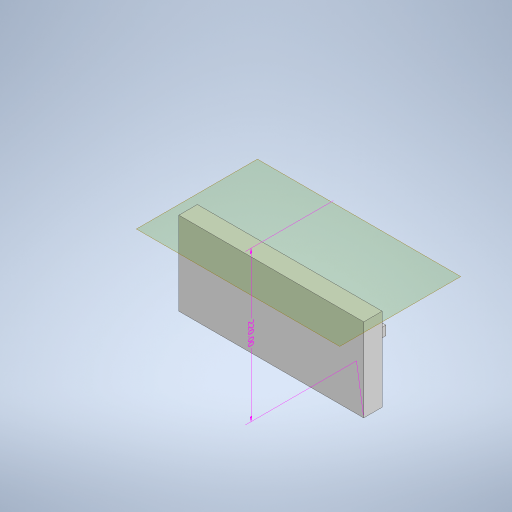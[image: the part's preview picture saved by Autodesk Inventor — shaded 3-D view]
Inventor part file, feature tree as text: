
AUTODESK INVENTOR PART (.ipt)
format: ipt  version: 2023 (Build 270158000, 158)  size: 312,832 bytes
history: native  units: mm
features: extrude x6, sketch x6, other x4, plane x3, split x1
ambient origin geometry x8: Origin, YZ Plane, XZ Plane, XY Plane, X Axis, Y Axis, Z Axis, Center Point
bodies: Body1 (feature_tree), Body2 (feature_tree)
feature tree (20):
  other  "Sólido1"
  other  "Anotaciones"
  extrude  "Extrusión1"  Depth=80.0mm
  extrude  "Extrusión2"  Depth=180.0mm
  extrude  "Extrusión3"  Depth=20.0mm
  extrude  "Extrusión4"  Depth=21.0mm
  plane  "Plano de trabajo1"
  extrude  "Extrusión6"  Depth=20.0mm
  plane  "Plano de trabajo3"
  extrude  "Extrusión7"  [1 undecoded]
  plane  "Plano de trabajo4"
  split  "Dividir1"
  sketch  "Boceto1"  dims[d0=200.0mm d1=80.0mm]
  sketch  "Boceto2"  dims[d2=130.0mm d3=0.0mm d4=180.0mm]
  sketch  "Boceto3"  dims[d5=60.0mm d6=20.0mm]
  sketch  "Boceto4"  dims[d7=60.0mm d8=0.0mm d9=21.0mm d10=43.0mm]
  sketch  "Boceto7"  dims[d11=43.0mm d12=0.0mm d13=20.0mm]
  other  "Sólido3"
  sketch  "Boceto10"  dims[d14=90.0mm d15=0.0mm d16=-90.0mm d28=20.0mm d29=20.0mm d30=30.0mm d31=30.0mm d32=20.0mm d33=35.0mm d34=35.0mm d35=69.0mm d36=10.0mm d37=0.0mm d45=1.5mm d50=10.0mm d51=0.0mm d52=10.0mm d53=89.5mm d54=90.0deg d38=3.166395mm d39=4.283575mm d40=220.0mm]
  other  "Cota lineal 1"
note: 1 required parameter value undecoded (feature->parameter linkage not recoverable at this tier; creation-order binding heuristic only, values carry confidence <= 0.55)
